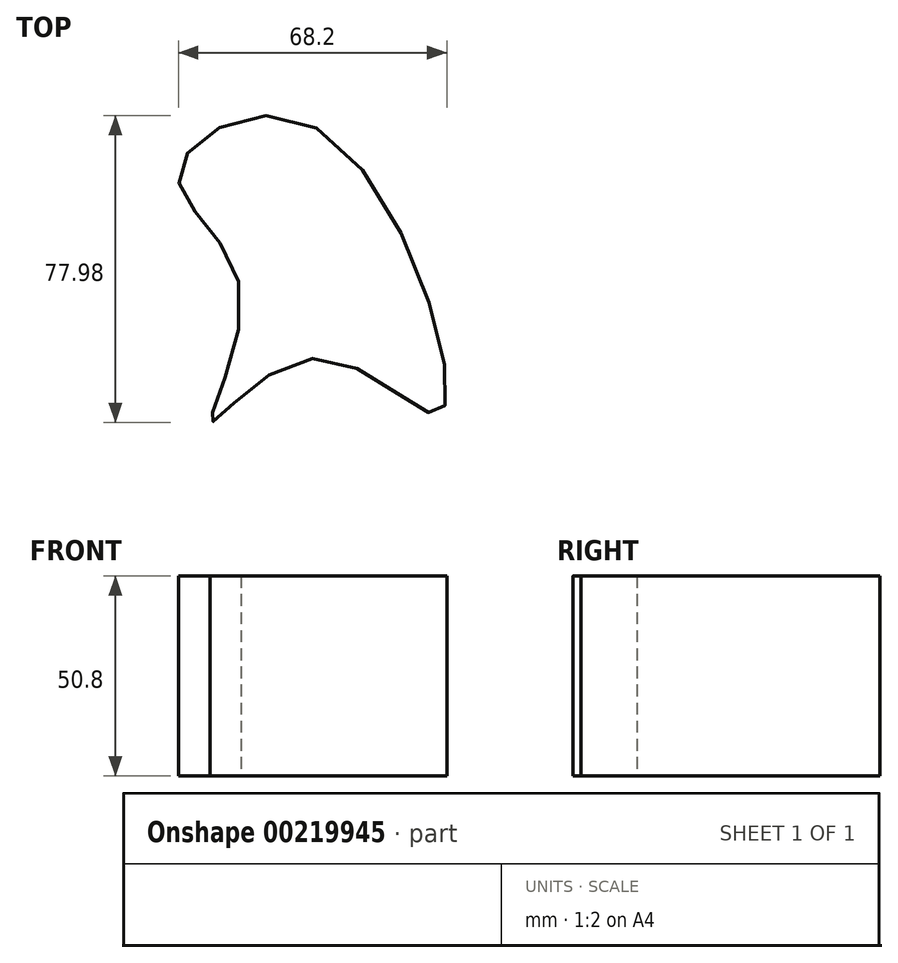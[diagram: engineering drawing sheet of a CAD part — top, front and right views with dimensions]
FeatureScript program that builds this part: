
annotation { "Feature Type Name" : "Feature", "Feature Type Description" : "" }
export const myFeature = defineFeature(function(context is Context, id is Id, definition is map)
    precondition{}
    {
        {
            var Q0;
            Q0=qCreatedBy(makeId("Top.planeOp"),FACE);
            var sketch = newSketch(context, id + "F0", { "sketchPlane" : qUnion([Q0])});
            skFitSpline(sketch, "E0", {"points": [v(0, 40.57) * mm, v(-35.01, 29.09) * mm, v(-19.45, 0) * mm, v(-26.86, -34.27) * mm, v(0, -17.97) * mm, v(31.68, -31.68) * mm, v(0, 40.57) * mm]});
            skSolve(sketch);
        }
        {
            var Q0;
            Q0 = qSketchRegion(id + "F0", true);
            extrude(context, id + "F1", {"entities" : qUnion([Q0]), "depth" : 50.8 * mm});
        }
    });
